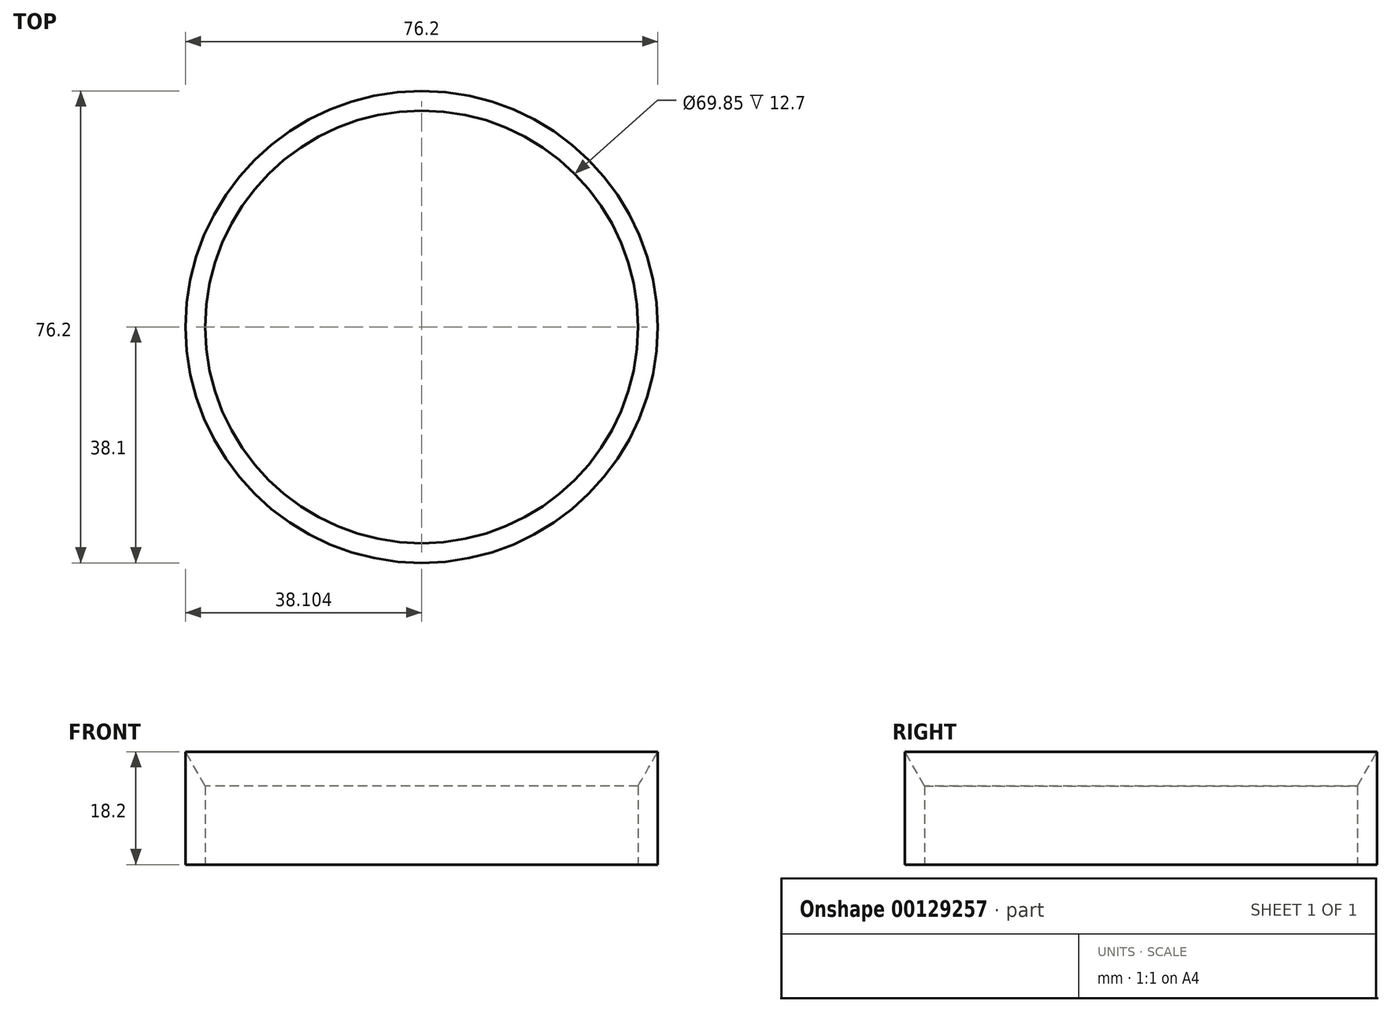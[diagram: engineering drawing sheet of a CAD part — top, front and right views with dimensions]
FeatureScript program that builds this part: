
annotation { "Feature Type Name" : "Feature", "Feature Type Description" : "" }
export const myFeature = defineFeature(function(context is Context, id is Id, definition is map)
    precondition{}
    {
        {
            var Q0;
            Q0=qCreatedBy(makeId("Top.planeOp"),FACE);
            var sketch = newSketch(context, id + "F0", { "sketchPlane" : qUnion([Q0])});
            skPoint(sketch, "E0", {"position": v(-38.14, -26.1) * mm});
            skCircle(sketch, "E1", {"center": v(-38.14, -26.1) * mm, "radius": 38.1 * mm});
            skCircle(sketch, "E2", {"center": v(-38.14, -26.1) * mm, "radius": 34.93 * mm});
            skCircle(sketch, "E3.0", {"center": v(-38.14, -26.1) * mm, "radius": 38.74 * mm});
            skSolve(sketch);
        }
        {
            var Q0;
            Q0=makeQuery(id+"F0.imprint","IMPRINT",FACE,{"disambiguationData":[TD([[makeQuery(id+"F0.imprint","IMPRINT",EDGE,{"derivedFrom":sQuery(id+"F0.wireOp",EDGE,"E1")}),1.0]])]});
            extrude(context, id + "F1", {"entities" : qUnion([Q0]), "depth" : 101.6 * mm});
        }
        {
            var Q0;
            Q0=makeQuery(id+"F1.opExtrude","CAP_EDGE",EDGE,{"disambiguationData":[OSD([sQuery(id+"F0.wireOp",EDGE,"E2")])],"isStart":false});
            chamfer(context, id + "F2", {"entities" : qUnion([Q0]), "chamferType" : ChamferType.OFFSET_ANGLE, "width" : 88.9 * mm, "oppositeDirection" : false, "angle" : 30 * degree, "tangentPropagation" : true});
        }
    });
